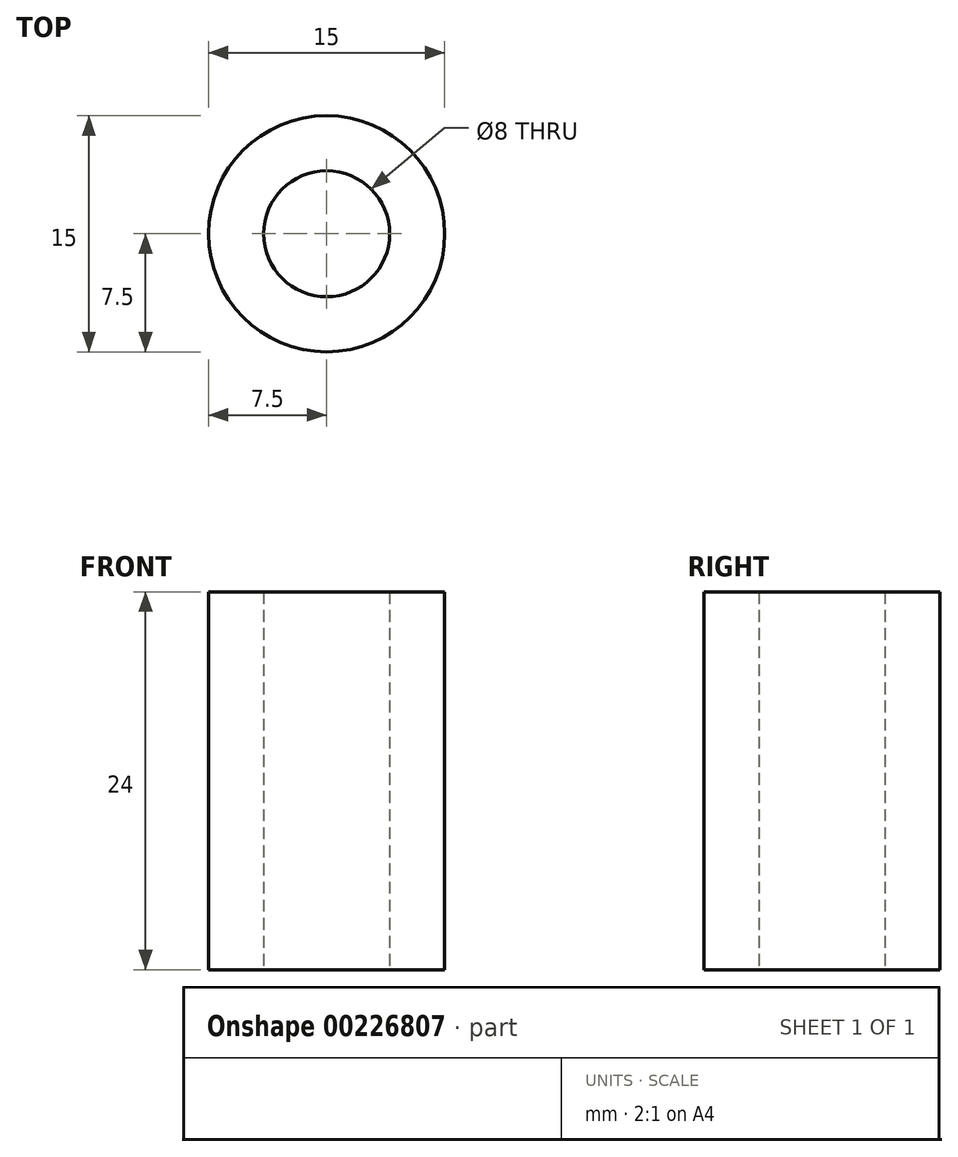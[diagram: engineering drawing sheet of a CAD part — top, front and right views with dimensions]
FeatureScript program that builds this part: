
annotation { "Feature Type Name" : "Feature", "Feature Type Description" : "" }
export const myFeature = defineFeature(function(context is Context, id is Id, definition is map)
    precondition{}
    {
        {
            var Q0;
            Q0=qCreatedBy(makeId("Top.planeOp"),FACE);
            var sketch = newSketch(context, id + "F0", { "sketchPlane" : qUnion([Q0])});
            skCircle(sketch, "E0", {"center": v(0, 0) * mm, "radius": 7.5 * mm});
            skCircle(sketch, "E1", {"center": v(0, 0) * mm, "radius": 4 * mm});
            skSolve(sketch);
        }
        {
            var Q0;
            Q0=makeQuery(id+"F0.imprint","IMPRINT",FACE,{"disambiguationData":[TD([[makeQuery(id+"F0.imprint","IMPRINT",EDGE,{"derivedFrom":sQuery(id+"F0.wireOp",EDGE,"E0")}),1.0]])]});
            extrude(context, id + "F1", {"entities" : qUnion([Q0]), "depth" : 24 * mm});
        }
    });
